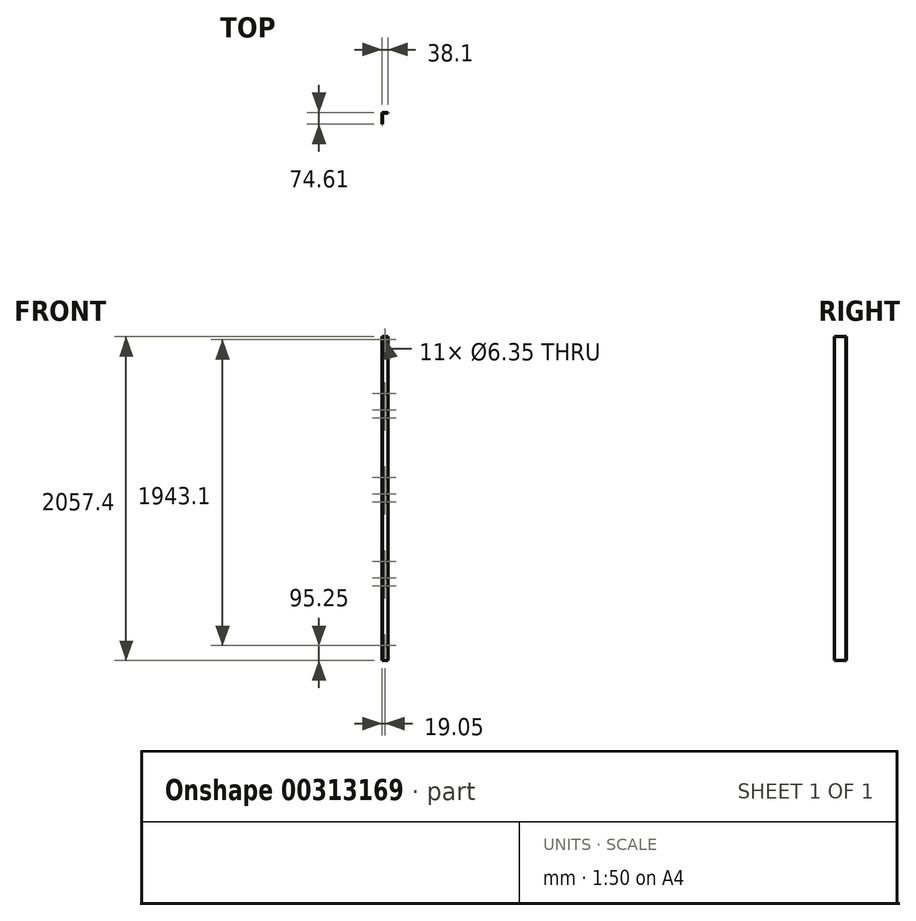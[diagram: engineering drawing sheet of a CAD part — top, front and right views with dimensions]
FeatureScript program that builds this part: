
annotation { "Feature Type Name" : "Feature", "Feature Type Description" : "" }
export const myFeature = defineFeature(function(context is Context, id is Id, definition is map)
    precondition{}
    {
        {
            var Q0;
            Q0=qCreatedBy(makeId("Top.planeOp"),FACE);
            var sketch = newSketch(context, id + "F0", { "sketchPlane" : qUnion([Q0])});
            skLineSegment(sketch, "E0.bottom", {"start": v(0, 0) * mm, "end": v(38.1, 0) * mm});
            skLineSegment(sketch, "E0.top", {"start": v(0, 74.61) * mm, "end": v(38.1, 74.61) * mm});
            skLineSegment(sketch, "E0.left", {"start": v(0, 0) * mm, "end": v(0, 74.61) * mm});
            skLineSegment(sketch, "E0.right", {"start": v(38.1, 0) * mm, "end": v(38.1, 74.61) * mm});
            skSolve(sketch);
        }
        {
            var Q0;
            Q0=qSketchRegion(id+"F0",true);
            extrude(context, id + "F1", {"entities" : qUnion([Q0]), "endBound" : BoundingType.SYMMETRIC, "depth" : 2057.4 * mm});
        }
        {
            var Q0;
            Q0=makeQuery(id+"F1.opExtrude","SWEPT_FACE",FACE,{"disambiguationData":[OSD([sQuery(id+"F0.wireOp",EDGE,"E0.right")])]});
            var Q1;
            Q1=makeQuery(id+"F1.opExtrude","CAP_FACE",FACE,{"disambiguationData":[OSD([sQuery(id+"F0.wireOp",EDGE,"E0.bottom"),sQuery(id+"F0.wireOp",EDGE,"E0.top"),sQuery(id+"F0.wireOp",EDGE,"E0.left"),sQuery(id+"F0.wireOp",EDGE,"E0.right")])],"isStart":false});
            var Q2;
            Q2=makeQuery(id+"F1.opExtrude","SWEPT_FACE",FACE,{"disambiguationData":[OSD([sQuery(id+"F0.wireOp",EDGE,"E0.bottom")])]});
            var Q3;
            Q3=makeQuery(id+"F1.opExtrude","CAP_FACE",FACE,{"disambiguationData":[OSD([sQuery(id+"F0.wireOp",EDGE,"E0.bottom"),sQuery(id+"F0.wireOp",EDGE,"E0.top"),sQuery(id+"F0.wireOp",EDGE,"E0.left"),sQuery(id+"F0.wireOp",EDGE,"E0.right")])],"isStart":true});
            shell(context, id + "F2", {"entities" : qUnion([Q0, Q1, Q2, Q3]), "thickness" : 2.78 * mm});
        }
        {
            var Q0;
            Q0=makeQuery(id+"F1.opExtrude","SWEPT_FACE",FACE,{"disambiguationData":[OSD([sQuery(id+"F0.wireOp",EDGE,"E0.top")])]});
            var sketch = newSketch(context, id + "F3", { "sketchPlane" : qUnion([Q0])});
            skCircle(sketch, "E1", {"center": v(-19.05, 561.98) * mm, "radius": 3.18 * mm});
            skCircle(sketch, "E2", {"center": v(-19.05, 511.18) * mm, "radius": 3.18 * mm});
            skCircle(sketch, "E3", {"center": v(-19.05, 133.35) * mm, "radius": 3.18 * mm});
            skCircle(sketch, "E4.0.1.0", {"center": v(-19.05, -22.23) * mm, "radius": 3.18 * mm});
            skCircle(sketch, "E4.0.1.1", {"center": v(-19.05, 28.57) * mm, "radius": 3.18 * mm});
            skCircle(sketch, "E4.0.1.2", {"center": v(-19.05, -400.05) * mm, "radius": 3.18 * mm});
            skCircle(sketch, "E4.0.2.0", {"center": v(-19.05, -555.63) * mm, "radius": 3.18 * mm});
            skCircle(sketch, "E4.0.2.1", {"center": v(-19.05, -504.83) * mm, "radius": 3.18 * mm});
            skCircle(sketch, "E4.0.2.2", {"center": v(-19.05, -933.45) * mm, "radius": 3.18 * mm});
            skLineSegment(sketch, "E4.direction1", {"start": v(-19.05, 133.35) * mm, "end": v(0, 133.35) * mm, "construction": true});
            skLineSegment(sketch, "E4.direction2", {"start": v(-19.05, 133.35) * mm, "end": v(-19.05, -400.05) * mm, "construction": true});
            skCircle(sketch, "E5", {"center": v(-19.05, 666.75) * mm, "radius": 3.18 * mm});
            skCircle(sketch, "E6", {"center": v(-19.05, 1009.65) * mm, "radius": 3.18 * mm});
            skSolve(sketch);
        }
        {
            var Q0;
            Q0=qSketchRegion(id+"F3",true);
            extrude(context, id + "F4", {"entities" : qUnion([Q0]), "operationType" : NewBodyOperationType.REMOVE, "endBound" : BoundingType.THROUGH_ALL, "oppositeDirection" : true, "depth" : 25.4 * mm});
        }
    });
